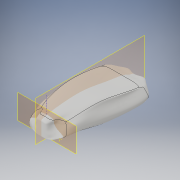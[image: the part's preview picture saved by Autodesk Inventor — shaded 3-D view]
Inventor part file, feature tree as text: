
AUTODESK INVENTOR PART (.ipt)
format: ipt  version: 2018 (Build 220112000, 112)  size: 524,288 bytes
history: native  units: in
note: dims shown in document units (in); Inventor stores cm internally (conversion verified against a paired STEP export)
features: plane x2, other x1, sketch x1
ambient origin geometry x8: Origin, YZ Plane, XZ Plane, XY Plane, X Axis, Y Axis, Z Axis, Center Point
bodies: Solid1 (feature_tree)
feature tree (4):
  other  "Form1"
  plane  "Work Plane1"
  sketch  "Sketch2"
  plane  "Work Plane2"
